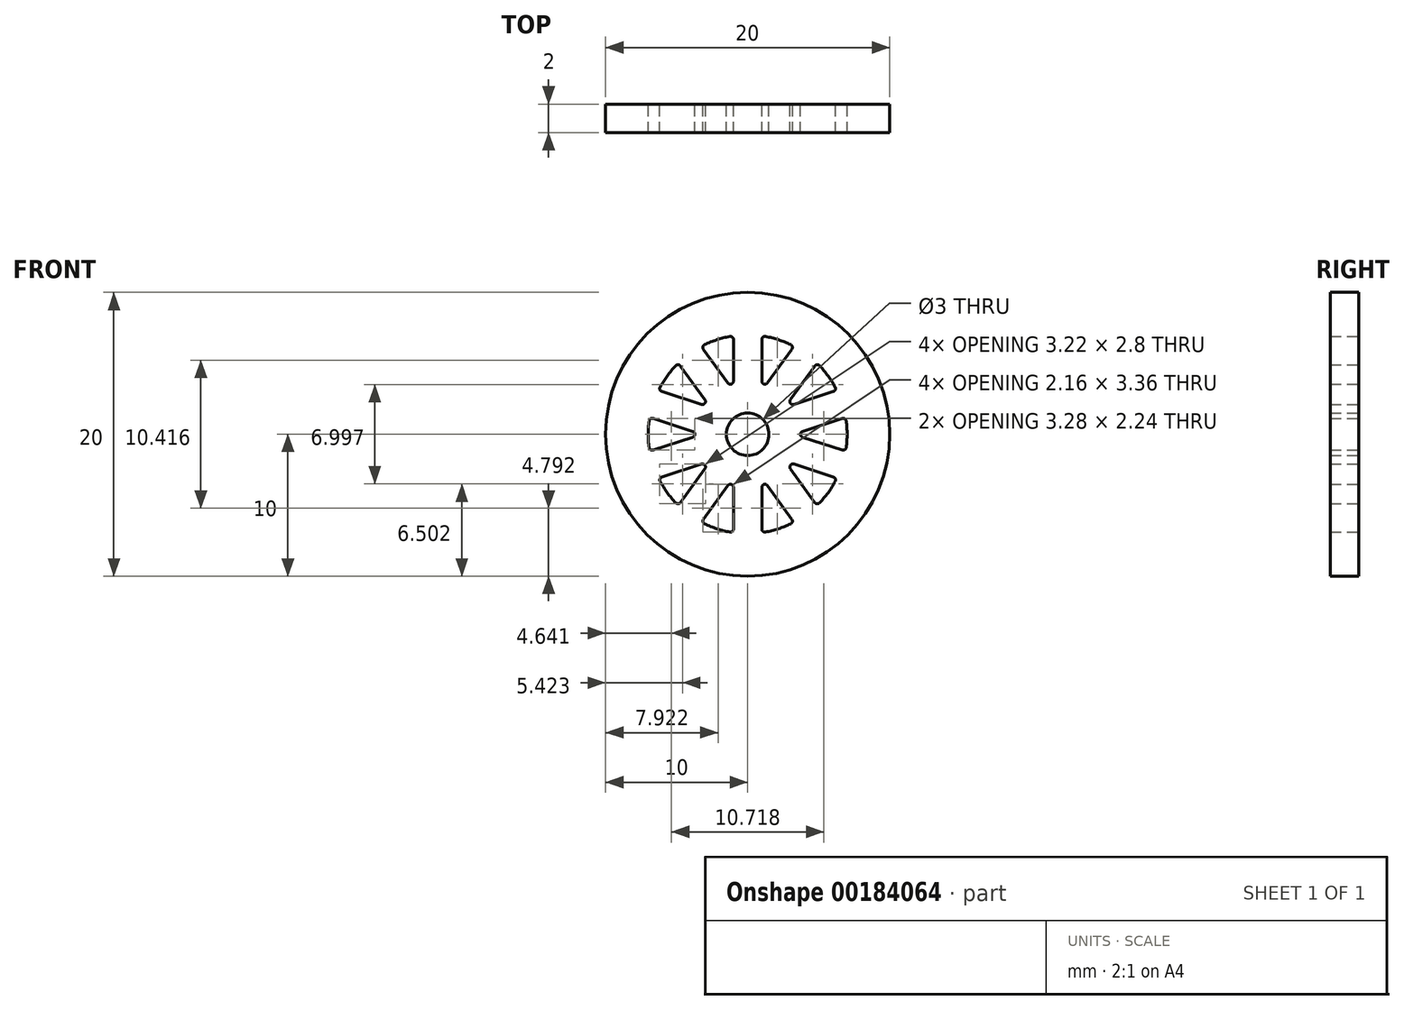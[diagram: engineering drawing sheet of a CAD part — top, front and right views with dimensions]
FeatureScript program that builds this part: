
annotation { "Feature Type Name" : "Feature", "Feature Type Description" : "" }
export const myFeature = defineFeature(function(context is Context, id is Id, definition is map)
    precondition{}
    {
        {
            var Q0;
            Q0=qCreatedBy(makeId("Front.planeOp"),FACE);
            var sketch = newSketch(context, id + "F0", { "sketchPlane" : qUnion([Q0])});
            skCircle(sketch, "E0", {"center": v(0, 0) * mm, "radius": 10 * mm});
            skArc(sketch, "E1.0", {"start": v(-6.94, 0.94) * mm, "mid": v(-7, 0) * mm, "end": v(-6.94, -0.94) * mm});
            skArc(sketch, "E2", {"start": v(-0.85, 2.88) * mm, "mid": v(-0.93, 2.85) * mm, "end": v(-1, 2.83) * mm});
            skCircle(sketch, "E3", {"center": v(0, 0) * mm, "radius": 1.5 * mm});
            skLineSegment(sketch, "E4", {"start": v(0, 1.5) * mm, "end": v(0, 0.72) * mm});
            skLineSegment(sketch, "E5.0", {"start": v(-1, 10) * mm, "end": v(-1, 9.95) * mm});
            skLineSegment(sketch, "E6.0", {"start": v(1, 10) * mm, "end": v(1, 9.95) * mm});
            skLineSegment(sketch, "E7.trimOffspring", {"start": v(-1, 6.67) * mm, "end": v(-1, 3.74) * mm});
            skLineSegment(sketch, "E8.trimOffspring", {"start": v(1, 6.67) * mm, "end": v(1, 3.74) * mm});
            skLineSegment(sketch, "E9.1.1", {"start": v(-3.11, 5.99) * mm, "end": v(-1.39, 3.61) * mm});
            skLineSegment(sketch, "E9.1.2", {"start": v(-4.73, 4.81) * mm, "end": v(-3, 2.44) * mm});
            skLineSegment(sketch, "E9.2.1", {"start": v(-6.04, 3.01) * mm, "end": v(-3.25, 2.1) * mm});
            skLineSegment(sketch, "E9.2.2", {"start": v(-6.66, 1.11) * mm, "end": v(-3.87, 0.2) * mm});
            skLineSegment(sketch, "E9.3.1", {"start": v(-6.66, -1.11) * mm, "end": v(-3.87, -0.2) * mm});
            skLineSegment(sketch, "E9.3.2", {"start": v(-6.04, -3.01) * mm, "end": v(-3.25, -2.1) * mm});
            skLineSegment(sketch, "E9.4.1", {"start": v(-4.73, -4.81) * mm, "end": v(-3, -2.44) * mm});
            skLineSegment(sketch, "E9.4.2", {"start": v(-3.11, -5.99) * mm, "end": v(-1.39, -3.61) * mm});
            skLineSegment(sketch, "E9.5.1", {"start": v(-1, -6.67) * mm, "end": v(-1, -3.74) * mm});
            skLineSegment(sketch, "E9.5.2", {"start": v(1, -6.67) * mm, "end": v(1, -3.74) * mm});
            skLineSegment(sketch, "E9.6.1", {"start": v(3.11, -5.99) * mm, "end": v(1.39, -3.61) * mm});
            skLineSegment(sketch, "E9.6.2", {"start": v(4.73, -4.81) * mm, "end": v(3, -2.44) * mm});
            skLineSegment(sketch, "E9.7.1", {"start": v(6.04, -3.01) * mm, "end": v(3.25, -2.1) * mm});
            skLineSegment(sketch, "E9.7.2", {"start": v(6.66, -1.11) * mm, "end": v(3.87, -0.2) * mm});
            skLineSegment(sketch, "E9.8.1", {"start": v(6.66, 1.11) * mm, "end": v(3.87, 0.2) * mm});
            skLineSegment(sketch, "E9.8.2", {"start": v(6.04, 3.01) * mm, "end": v(3.25, 2.1) * mm});
            skLineSegment(sketch, "E9.9.1", {"start": v(4.73, 4.81) * mm, "end": v(3, 2.44) * mm});
            skLineSegment(sketch, "E9.9.2", {"start": v(3.11, 5.99) * mm, "end": v(1.39, 3.61) * mm});
            skPoint(sketch, "E10.orphan", {"position": v(-9.51, 3.1) * mm});
            skPoint(sketch, "E11.orphan", {"position": v(-9.51, -3.1) * mm});
            skPoint(sketch, "E12.orphan", {"position": v(-5.88, -8.1) * mm});
            skPoint(sketch, "E13.orphan", {"position": v(0, -10) * mm});
            skPoint(sketch, "E14.orphan", {"position": v(5.88, -8.1) * mm});
            skPoint(sketch, "E15.orphan", {"position": v(9.51, -3.1) * mm});
            skPoint(sketch, "E16.orphan", {"position": v(9.51, 3.1) * mm});
            skPoint(sketch, "E17.orphan", {"position": v(5.88, 8.1) * mm});
            skPoint(sketch, "E18.orphan", {"position": v(-5.88, 8.1) * mm});
            skPoint(sketch, "E19.orphan", {"position": v(0, 10) * mm});
            skArc(sketch, "E20.trimOffspring", {"start": v(6.16, 3.32) * mm, "mid": v(5.66, 4.11) * mm, "end": v(5.06, 4.83) * mm});
            skArc(sketch, "E21.trimOffspring", {"start": v(1, 2.83) * mm, "mid": v(0.93, 2.85) * mm, "end": v(0.85, 2.88) * mm});
            skArc(sketch, "E22.trimOffspring", {"start": v(2.47, 1.7) * mm, "mid": v(2.43, 1.76) * mm, "end": v(2.38, 1.83) * mm});
            skArc(sketch, "E23.trimOffspring", {"start": v(-3, 0.08) * mm, "mid": v(-3, 0) * mm, "end": v(-3, -0.08) * mm});
            skArc(sketch, "E24.trimOffspring", {"start": v(-2.47, -1.7) * mm, "mid": v(-2.43, -1.76) * mm, "end": v(-2.38, -1.83) * mm});
            skArc(sketch, "E25.trimOffspring", {"start": v(-2.38, 1.83) * mm, "mid": v(-2.43, 1.76) * mm, "end": v(-2.47, 1.7) * mm});
            skArc(sketch, "E26.trimOffspring", {"start": v(-1, -2.83) * mm, "mid": v(-0.93, -2.85) * mm, "end": v(-0.85, -2.88) * mm});
            skArc(sketch, "E27.trimOffspring", {"start": v(0.85, -2.88) * mm, "mid": v(0.93, -2.85) * mm, "end": v(1, -2.83) * mm});
            skArc(sketch, "E28.trimOffspring", {"start": v(1.25, -6.89) * mm, "mid": v(2.16, -6.66) * mm, "end": v(3.03, -6.3) * mm});
            skArc(sketch, "E29.trimOffspring", {"start": v(-3.03, -6.3) * mm, "mid": v(-2.16, -6.66) * mm, "end": v(-1.25, -6.89) * mm});
            skArc(sketch, "E30.trimOffspring", {"start": v(-6.16, -3.32) * mm, "mid": v(-5.66, -4.11) * mm, "end": v(-5.06, -4.83) * mm});
            skArc(sketch, "E31.trimOffspring", {"start": v(-5.06, 4.83) * mm, "mid": v(-5.66, 4.11) * mm, "end": v(-6.16, 3.32) * mm});
            skArc(sketch, "E32.trimOffspring", {"start": v(-1.25, 6.89) * mm, "mid": v(-2.16, 6.66) * mm, "end": v(-3.03, 6.3) * mm});
            skArc(sketch, "E33.trimOffspring", {"start": v(3.03, 6.3) * mm, "mid": v(2.16, 6.66) * mm, "end": v(1.25, 6.89) * mm});
            skArc(sketch, "E34.trimOffspring", {"start": v(6.94, -0.94) * mm, "mid": v(7, 0) * mm, "end": v(6.94, 0.94) * mm});
            skArc(sketch, "E35.trimOffspring", {"start": v(5.06, -4.83) * mm, "mid": v(5.66, -4.11) * mm, "end": v(6.16, -3.32) * mm});
            skArc(sketch, "E36.trimOffspring", {"start": v(3, -0.08) * mm, "mid": v(3, 0) * mm, "end": v(3, 0.08) * mm});
            skArc(sketch, "E37.trimOffspring", {"start": v(2.38, -1.83) * mm, "mid": v(2.43, -1.76) * mm, "end": v(2.47, -1.7) * mm});
            skPoint(sketch, "E38.visualSharp", {"position": v(-3.26, 6.2) * mm});
            skArc(sketch, "E38.filletArc", {"start": v(-3.03, 6.3) * mm, "mid": v(-3.15, 6.17) * mm, "end": v(-3.11, 5.99) * mm});
            skPoint(sketch, "E39.visualSharp", {"position": v(-1, 6.93) * mm});
            skArc(sketch, "E39.filletArc", {"start": v(-1, 6.67) * mm, "mid": v(-1.08, 6.84) * mm, "end": v(-1.25, 6.89) * mm});
            skPoint(sketch, "E40.newPointA", {"position": v(-1, 2.83) * mm});
            skPoint(sketch, "E40.newPointB", {"position": v(-0.85, 2.88) * mm});
            skArc(sketch, "E40.filletArc", {"start": v(-1.03, 3.12) * mm, "mid": v(-1.01, 3.11) * mm, "end": v(-1, 3.13) * mm});
            skPoint(sketch, "E41.visualSharp", {"position": v(-4.88, 5.02) * mm});
            skArc(sketch, "E41.filletArc", {"start": v(-4.73, 4.81) * mm, "mid": v(-4.9, 4.9) * mm, "end": v(-5.06, 4.83) * mm});
            skPoint(sketch, "E42.visualSharp", {"position": v(-6.28, 3.1) * mm});
            skArc(sketch, "E42.filletArc", {"start": v(-6.16, 3.32) * mm, "mid": v(-6.17, 3.14) * mm, "end": v(-6.04, 3.01) * mm});
            skPoint(sketch, "E43.newPointA", {"position": v(-2.47, 1.7) * mm});
            skPoint(sketch, "E43.newPointB", {"position": v(-2.38, 1.83) * mm});
            skArc(sketch, "E43.filletArc", {"start": v(-3.25, 2.1) * mm, "mid": v(-3, 2.19) * mm, "end": v(-3, 2.44) * mm});
            skPoint(sketch, "E44.newPointA", {"position": v(-3, -0.08) * mm});
            skPoint(sketch, "E44.newPointB", {"position": v(-3, 0.08) * mm});
            skArc(sketch, "E44.filletArc", {"start": v(-3.87, -0.2) * mm, "mid": v(-3.72, 0) * mm, "end": v(-3.87, 0.2) * mm});
            skArc(sketch, "E45.filletArc", {"start": v(-1.39, 3.61) * mm, "mid": v(-1.15, 3.54) * mm, "end": v(-1, 3.74) * mm});
            skPoint(sketch, "E46.visualSharp", {"position": v(-6.28, -3.1) * mm});
            skArc(sketch, "E46.filletArc", {"start": v(-6.04, -3.01) * mm, "mid": v(-6.17, -3.14) * mm, "end": v(-6.16, -3.32) * mm});
            skPoint(sketch, "E47.visualSharp", {"position": v(-4.88, -5.02) * mm});
            skArc(sketch, "E47.filletArc", {"start": v(-5.06, -4.83) * mm, "mid": v(-4.9, -4.9) * mm, "end": v(-4.73, -4.81) * mm});
            skPoint(sketch, "E48.newPointA", {"position": v(-2.38, -1.83) * mm});
            skPoint(sketch, "E48.newPointB", {"position": v(-2.47, -1.7) * mm});
            skArc(sketch, "E48.filletArc", {"start": v(-3, -2.44) * mm, "mid": v(-3, -2.19) * mm, "end": v(-3.25, -2.1) * mm});
            skPoint(sketch, "E49.newPointA", {"position": v(-0.85, -2.88) * mm});
            skPoint(sketch, "E49.newPointB", {"position": v(-1, -2.83) * mm});
            skArc(sketch, "E49.filletArc", {"start": v(-1, -3.74) * mm, "mid": v(-1.15, -3.54) * mm, "end": v(-1.39, -3.61) * mm});
            skPoint(sketch, "E50.visualSharp", {"position": v(-1, -6.93) * mm});
            skArc(sketch, "E50.filletArc", {"start": v(-1.25, -6.89) * mm, "mid": v(-1.08, -6.84) * mm, "end": v(-1, -6.67) * mm});
            skPoint(sketch, "E51.visualSharp", {"position": v(-3.26, -6.2) * mm});
            skArc(sketch, "E51.filletArc", {"start": v(-3.11, -5.99) * mm, "mid": v(-3.15, -6.17) * mm, "end": v(-3.03, -6.3) * mm});
            skPoint(sketch, "E52.visualSharp", {"position": v(-6.9, 1.19) * mm});
            skArc(sketch, "E52.filletArc", {"start": v(-6.66, 1.11) * mm, "mid": v(-6.84, 1.09) * mm, "end": v(-6.94, 0.94) * mm});
            skPoint(sketch, "E53.visualSharp", {"position": v(-6.9, -1.19) * mm});
            skArc(sketch, "E53.filletArc", {"start": v(-6.94, -0.94) * mm, "mid": v(-6.84, -1.09) * mm, "end": v(-6.66, -1.11) * mm});
            skPoint(sketch, "E54.visualSharp", {"position": v(1, -6.93) * mm});
            skArc(sketch, "E54.filletArc", {"start": v(1, -6.67) * mm, "mid": v(1.08, -6.84) * mm, "end": v(1.25, -6.89) * mm});
            skPoint(sketch, "E55.visualSharp", {"position": v(3.26, -6.2) * mm});
            skArc(sketch, "E55.filletArc", {"start": v(3.03, -6.3) * mm, "mid": v(3.15, -6.17) * mm, "end": v(3.11, -5.99) * mm});
            skPoint(sketch, "E56.newPointA", {"position": v(0.85, -2.88) * mm});
            skPoint(sketch, "E56.newPointB", {"position": v(1, -2.83) * mm});
            skArc(sketch, "E56.filletArc", {"start": v(1.39, -3.61) * mm, "mid": v(1.15, -3.54) * mm, "end": v(1, -3.74) * mm});
            skPoint(sketch, "E57.visualSharp", {"position": v(4.88, -5.02) * mm});
            skArc(sketch, "E57.filletArc", {"start": v(4.73, -4.81) * mm, "mid": v(4.9, -4.9) * mm, "end": v(5.06, -4.83) * mm});
            skPoint(sketch, "E58.visualSharp", {"position": v(6.28, -3.1) * mm});
            skArc(sketch, "E58.filletArc", {"start": v(6.16, -3.32) * mm, "mid": v(6.17, -3.14) * mm, "end": v(6.04, -3.01) * mm});
            skPoint(sketch, "E59.newPointA", {"position": v(2.47, -1.7) * mm});
            skPoint(sketch, "E59.newPointB", {"position": v(2.38, -1.83) * mm});
            skArc(sketch, "E59.filletArc", {"start": v(3.25, -2.1) * mm, "mid": v(3, -2.19) * mm, "end": v(3, -2.44) * mm});
            skPoint(sketch, "E60.visualSharp", {"position": v(6.9, -1.19) * mm});
            skArc(sketch, "E60.filletArc", {"start": v(6.66, -1.11) * mm, "mid": v(6.84, -1.09) * mm, "end": v(6.94, -0.94) * mm});
            skPoint(sketch, "E61.visualSharp", {"position": v(6.9, 1.19) * mm});
            skArc(sketch, "E61.filletArc", {"start": v(6.94, 0.94) * mm, "mid": v(6.84, 1.09) * mm, "end": v(6.66, 1.11) * mm});
            skPoint(sketch, "E62.newPointA", {"position": v(3, -0.08) * mm});
            skPoint(sketch, "E62.newPointB", {"position": v(3, 0.08) * mm});
            skArc(sketch, "E62.filletArc", {"start": v(3.87, 0.2) * mm, "mid": v(3.72, 0) * mm, "end": v(3.87, -0.2) * mm});
            skPoint(sketch, "E63.visualSharp", {"position": v(6.28, 3.1) * mm});
            skArc(sketch, "E63.filletArc", {"start": v(6.04, 3.01) * mm, "mid": v(6.17, 3.14) * mm, "end": v(6.16, 3.32) * mm});
            skPoint(sketch, "E64.newPointA", {"position": v(2.38, 1.83) * mm});
            skPoint(sketch, "E64.newPointB", {"position": v(2.47, 1.7) * mm});
            skArc(sketch, "E64.filletArc", {"start": v(3, 2.44) * mm, "mid": v(3, 2.19) * mm, "end": v(3.25, 2.1) * mm});
            skPoint(sketch, "E65.visualSharp", {"position": v(4.88, 5.02) * mm});
            skArc(sketch, "E65.filletArc", {"start": v(5.06, 4.83) * mm, "mid": v(4.9, 4.9) * mm, "end": v(4.73, 4.81) * mm});
            skPoint(sketch, "E66.visualSharp", {"position": v(3.26, 6.2) * mm});
            skArc(sketch, "E66.filletArc", {"start": v(3.11, 5.99) * mm, "mid": v(3.15, 6.17) * mm, "end": v(3.03, 6.3) * mm});
            skPoint(sketch, "E67.newPointA", {"position": v(0.85, 2.88) * mm});
            skPoint(sketch, "E67.newPointB", {"position": v(1, 2.83) * mm});
            skArc(sketch, "E67.filletArc", {"start": v(1, 3.74) * mm, "mid": v(1.15, 3.54) * mm, "end": v(1.39, 3.61) * mm});
            skPoint(sketch, "E68.visualSharp", {"position": v(1, 6.93) * mm});
            skArc(sketch, "E68.filletArc", {"start": v(1.25, 6.89) * mm, "mid": v(1.08, 6.84) * mm, "end": v(1, 6.67) * mm});
            skSolve(sketch);
        }
        {
            var Q0;
            Q0=qSketchRegion(id+"F0",true);
            extrude(context, id + "F1", {"entities" : qUnion([Q0]), "endBound" : BoundingType.SYMMETRIC, "depth" : 2 * mm});
        }
    });
